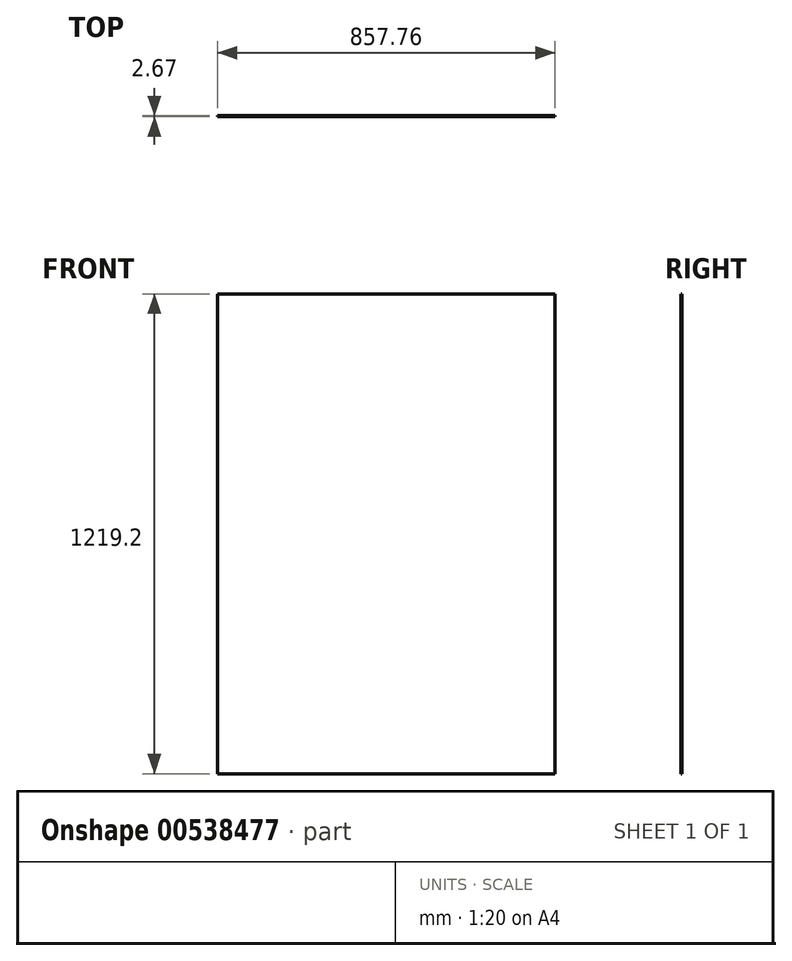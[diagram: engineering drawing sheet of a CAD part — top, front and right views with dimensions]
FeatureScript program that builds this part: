
annotation { "Feature Type Name" : "Feature", "Feature Type Description" : "" }
export const myFeature = defineFeature(function(context is Context, id is Id, definition is map)
    precondition{}
    {
        {
            var Q0;
            Q0=qCreatedBy(makeId("Front.planeOp"),FACE);
            var sketch = newSketch(context, id + "F0", { "sketchPlane" : qUnion([Q0])});
            skLineSegment(sketch, "E0.bottom", {"start": v(0, 0) * mm, "end": v(857.76, 0) * mm});
            skLineSegment(sketch, "E0.top", {"start": v(0, 1219.2) * mm, "end": v(857.76, 1219.2) * mm});
            skLineSegment(sketch, "E0.left", {"start": v(0, 0) * mm, "end": v(0, 1219.2) * mm});
            skLineSegment(sketch, "E0.right", {"start": v(857.76, 0) * mm, "end": v(857.76, 1219.2) * mm});
            skSolve(sketch);
        }
        {
            var Q0;
            Q0 = qSketchRegion(id + "F0", true);
            extrude(context, id + "F1", {"entities" : qUnion([Q0]), "depth" : 2.67 * mm, "offsetDistance" : 25.4 * mm});
        }
    });
